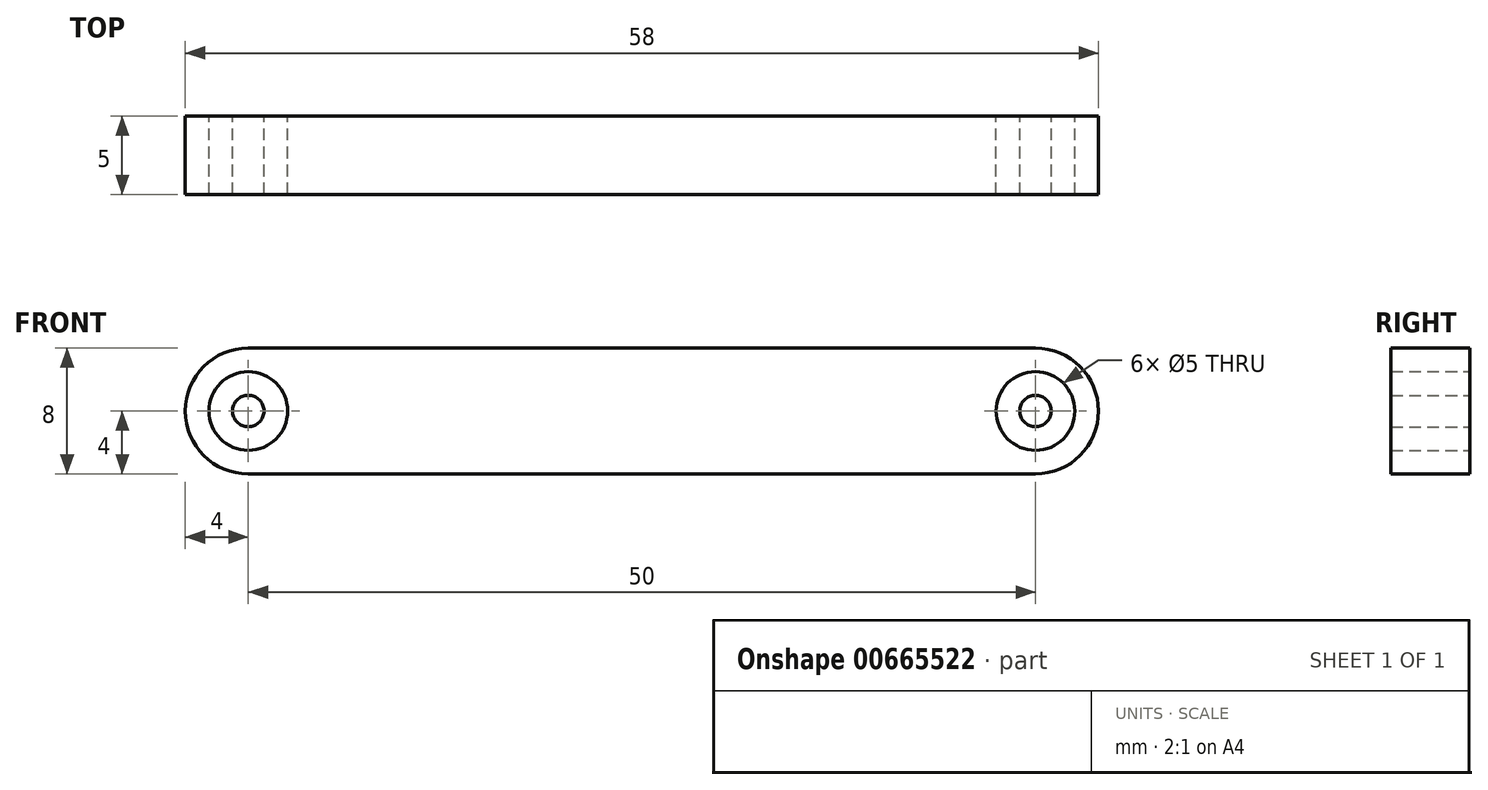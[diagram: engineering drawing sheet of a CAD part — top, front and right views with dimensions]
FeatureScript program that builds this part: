
annotation { "Feature Type Name" : "Feature", "Feature Type Description" : "" }
export const myFeature = defineFeature(function(context is Context, id is Id, definition is map)
    precondition{}
    {
        {
            var Q0;
            Q0=qCreatedBy(makeId("Front.planeOp"),FACE);
            var sketch = newSketch(context, id + "F0", { "sketchPlane" : qUnion([Q0])});
            skArc(sketch, "E0", {"start": v(0, 4) * mm, "mid": v(-4, 0) * mm, "end": v(0, -4) * mm});
            skArc(sketch, "E1", {"start": v(50, -4) * mm, "mid": v(54, 0) * mm, "end": v(50, 4) * mm});
            skLineSegment(sketch, "E2", {"start": v(0, 4) * mm, "end": v(50, 4) * mm});
            skLineSegment(sketch, "E3", {"start": v(0, -4) * mm, "end": v(50, -4) * mm});
            skCircle(sketch, "E4", {"center": v(0, 0) * mm, "radius": 2.5 * mm});
            skCircle(sketch, "E5", {"center": v(50, 0) * mm, "radius": 2.5 * mm});
            skCircle(sketch, "E6", {"center": v(0, 0) * mm, "radius": 1 * mm});
            skCircle(sketch, "E7", {"center": v(50, 0) * mm, "radius": 1 * mm});
            skSolve(sketch);
        }
        {
            var Q0;
            Q0 = qSketchRegion(id + "F0", true);
            var Q1;
            Q1=makeQuery(id+"F0.imprint","IMPRINT",FACE,{"disambiguationData":[TD([[makeQuery(id+"F0.imprint","IMPRINT",EDGE,{"derivedFrom":sQuery(id+"F0.wireOp",EDGE,"E6")}),1.0]])]});
            var Q2;
            Q2=makeQuery(id+"F0.imprint","IMPRINT",FACE,{"disambiguationData":[TD([[makeQuery(id+"F0.imprint","IMPRINT",EDGE,{"derivedFrom":sQuery(id+"F0.wireOp",EDGE,"E7")}),1.0]])]});
            extrude(context, id + "F1", {"entities" : qUnion([Q0, Q1, Q2]), "depth" : 5 * mm, "offsetDistance" : 25.4 * mm});
        }
    });
